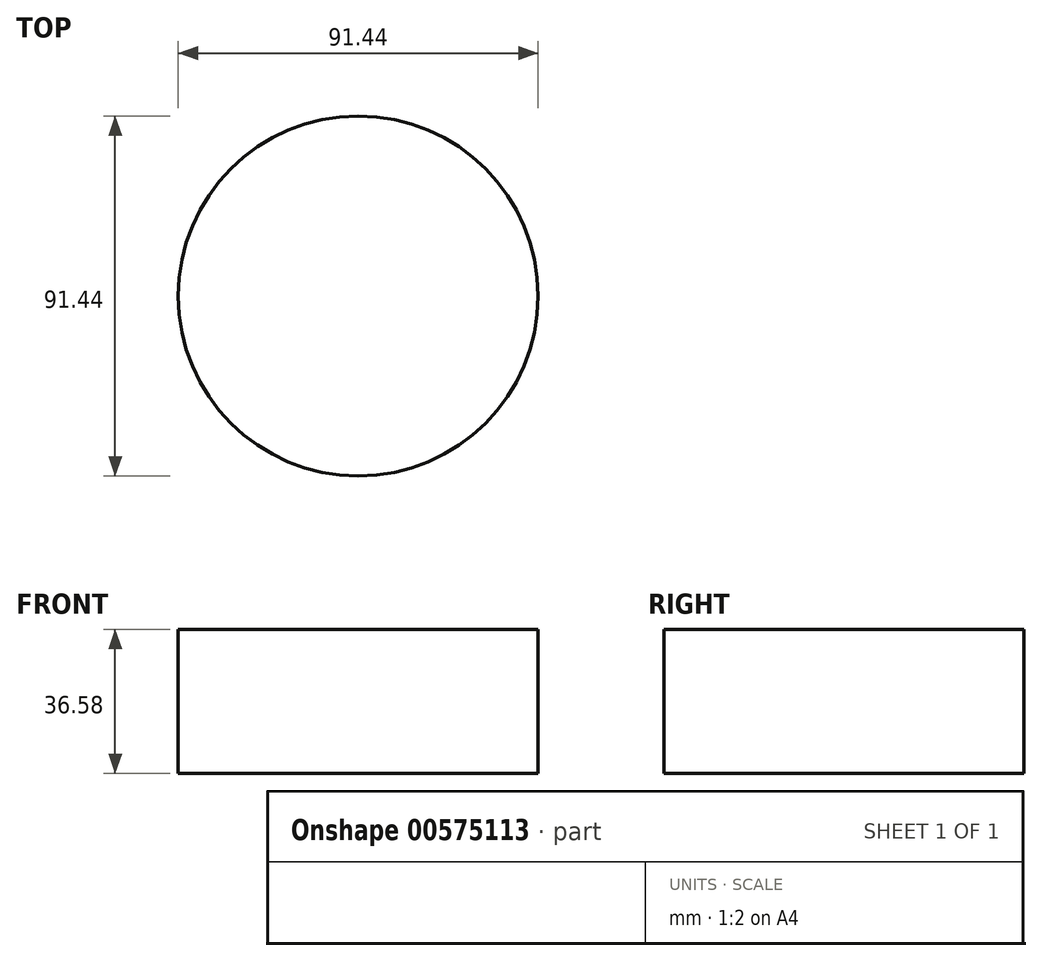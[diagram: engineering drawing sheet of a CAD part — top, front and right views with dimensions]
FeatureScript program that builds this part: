
annotation { "Feature Type Name" : "Feature", "Feature Type Description" : "" }
export const myFeature = defineFeature(function(context is Context, id is Id, definition is map)
    precondition{}
    {
        {
            var Q0;
            Q0=qCreatedBy(makeId("Top.planeOp"),FACE);
            var sketch = newSketch(context, id + "F0", { "sketchPlane" : qUnion([Q0])});
            skCircle(sketch, "E0", {"center": v(0, 0) * mm, "radius": 45.72 * mm});
            skSolve(sketch);
        }
        {
            var Q0;
            Q0=makeQuery(id+"F0.imprint","IMPRINT",FACE,{"disambiguationData":[TD([[makeQuery(id+"F0.imprint","IMPRINT",EDGE,{"derivedFrom":sQuery(id+"F0.wireOp",EDGE,"E0")}),1.0]])]});
            extrude(context, id + "F1", {"entities" : qUnion([Q0]), "depth" : 0.04 * yard, "offsetDistance" : 0.03 * yard});
        }
        {
            var Q0;
            Q0=makeQuery(id+"F1.opExtrude","CAP_FACE",FACE,{"disambiguationData":[OSD([sQuery(id+"F0.wireOp",EDGE,"E0")])],"isStart":true});
            var sketch = newSketch(context, id + "F2", { "sketchPlane" : qUnion([Q0])});
            skLineSegment(sketch, "E1.bottom", {"start": v(54.86, 54.86) * mm, "end": v(-54.86, 54.86) * mm});
            skLineSegment(sketch, "E1.top", {"start": v(54.86, -54.86) * mm, "end": v(-54.86, -54.86) * mm});
            skLineSegment(sketch, "E1.left", {"start": v(54.86, 54.86) * mm, "end": v(54.86, -54.86) * mm});
            skLineSegment(sketch, "E1.right", {"start": v(-54.86, 54.86) * mm, "end": v(-54.86, -54.86) * mm});
            skPoint(sketch, "E1.middle", {"position": v(0, 0) * mm});
            skSolve(sketch);
        }
        {
            var Q0;
            Q0=makeQuery(id+"F2.imprint","IMPRINT",FACE,{"disambiguationData":[TD([[makeQuery(id+"F2.imprint","IMPRINT",EDGE,{"derivedFrom":sQuery(id+"F2.wireOp",EDGE,"E1.bottom")}),1.0]])]});
            extrude(context, id + "F3", {"entities" : qUnion([Q0]), "depth" : 0.03 * yard, "offsetDistance" : 0.03 * yard});
        }
        {
            var Q0;
            Q0=makeQuery(id+"F3.opExtrude","SWEPT_BODY",BODY,{"disambiguationData":[OSD([sQuery(id+"F0.wireOp",EDGE,"E0"),sQuery(id+"F2.wireOp",EDGE,"E1.bottom"),sQuery(id+"F2.wireOp",EDGE,"E1.top"),sQuery(id+"F2.wireOp",EDGE,"E1.left"),sQuery(id+"F2.wireOp",EDGE,"E1.right")])]});
            deleteBodies(context, id + "F4", {"entities" : qUnion([Q0])});
        }
    });
